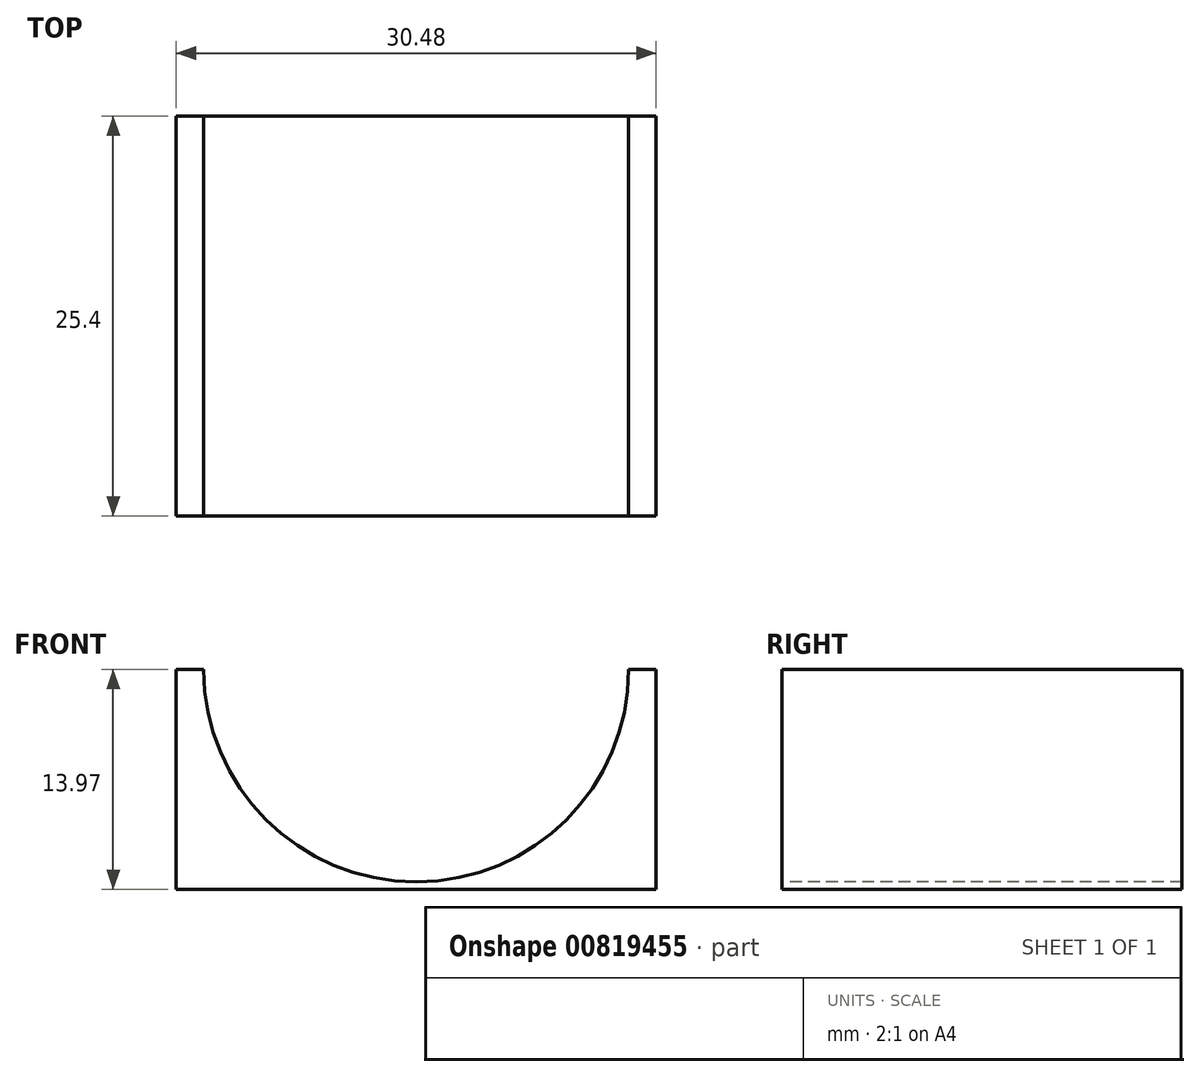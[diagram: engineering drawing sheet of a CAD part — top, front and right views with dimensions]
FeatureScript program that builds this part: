
annotation { "Feature Type Name" : "Feature", "Feature Type Description" : "" }
export const myFeature = defineFeature(function(context is Context, id is Id, definition is map)
    precondition{}
    {
        {
            var Q0;
            Q0=qCreatedBy(makeId("Front.planeOp"),FACE);
            var sketch = newSketch(context, id + "F0", { "sketchPlane" : qUnion([Q0])});
            skLineSegment(sketch, "E0.bottom", {"start": v(15.24, -13.97) * mm, "end": v(-15.24, -13.97) * mm});
            skLineSegment(sketch, "E0.top", {"start": v(15.24, 13.97) * mm, "end": v(-15.24, 13.97) * mm});
            skLineSegment(sketch, "E0.left", {"start": v(15.24, -13.97) * mm, "end": v(15.24, 13.97) * mm});
            skLineSegment(sketch, "E0.right", {"start": v(-15.24, -13.97) * mm, "end": v(-15.24, 13.97) * mm});
            skPoint(sketch, "E0.middle", {"position": v(0, 0) * mm});
            skSolve(sketch);
        }
        {
            var Q0;
            Q0=makeQuery(id+"F0.imprint","IMPRINT",FACE,{"disambiguationData":[TD([[makeQuery(id+"F0.imprint","IMPRINT",EDGE,{"derivedFrom":sQuery(id+"F0.wireOp",EDGE,"E0.bottom")}),-1.0]])]});
            extrude(context, id + "F1", {"entities" : qUnion([Q0]), "depth" : 25.4 * mm, "offsetDistance" : 25.4 * mm, "symmetric" : true});
        }
        {
            var Q0;
            Q0=makeQuery(id+"F1.opExtrude","CAP_FACE",FACE,{"disambiguationData":[OSD([sQuery(id+"F0.wireOp",EDGE,"E0.bottom"),sQuery(id+"F0.wireOp",EDGE,"E0.top"),sQuery(id+"F0.wireOp",EDGE,"E0.left"),sQuery(id+"F0.wireOp",EDGE,"E0.right")])],"isStart":false});
            var sketch = newSketch(context, id + "F2", { "sketchPlane" : qUnion([Q0])});
            skCircle(sketch, "E1", {"center": v(0, 0) * mm, "radius": 13.5 * mm});
            skSolve(sketch);
        }
        {
            var Q0;
            {var subQ0=sQuery(id+"F2.wireOp",EDGE,"E1");var subQ1=makeQuery(id+"F2.imprint","INTERSECT",VERTEX,{"derivedFrom":[makeQuery(id+"F1.opExtrude","CAP_EDGE",EDGE,{"disambiguationData":[OSD([sQuery(id+"F0.wireOp",EDGE,"E0.top")])],"isStart":false}),subQ0]});Q0=makeQuery(id+"F2.imprint","IMPRINT",FACE,{"disambiguationData":[TD([[makeQuery(id+"F2.imprint","IMPRINT",EDGE,{"disambiguationData":[TD([[subQ1,1.0]])],"derivedFrom":subQ0}),1.0]])]});}
            extrude(context, id + "F3", {"entities" : qUnion([Q0]), "operationType" : NewBodyOperationType.REMOVE, "oppositeDirection" : true, "depth" : 25.4 * mm, "offsetDistance" : 25.4 * mm});
        }
        {
            var Q0;
            Q0=qCreatedBy(makeId("Front.planeOp"),FACE);
            var sketch = newSketch(context, id + "F4", { "sketchPlane" : qUnion([Q0])});
            skLineSegment(sketch, "E2.bottom", {"start": v(-30.37, 0) * mm, "end": v(38.17, 0) * mm});
            skLineSegment(sketch, "E2.top", {"start": v(-30.37, 31.44) * mm, "end": v(38.17, 31.44) * mm});
            skLineSegment(sketch, "E2.left", {"start": v(-30.37, 0) * mm, "end": v(-30.37, 31.44) * mm});
            skLineSegment(sketch, "E2.right", {"start": v(38.17, 0) * mm, "end": v(38.17, 31.44) * mm});
            skSolve(sketch);
        }
        {
            var Q0;
            Q0 = qSketchRegion(id + "F4", true);
            extrude(context, id + "F5", {"entities" : qUnion([Q0]), "operationType" : NewBodyOperationType.REMOVE, "depth" : 25.4 * mm, "offsetDistance" : 25.4 * mm, "symmetric" : true});
        }
    });
